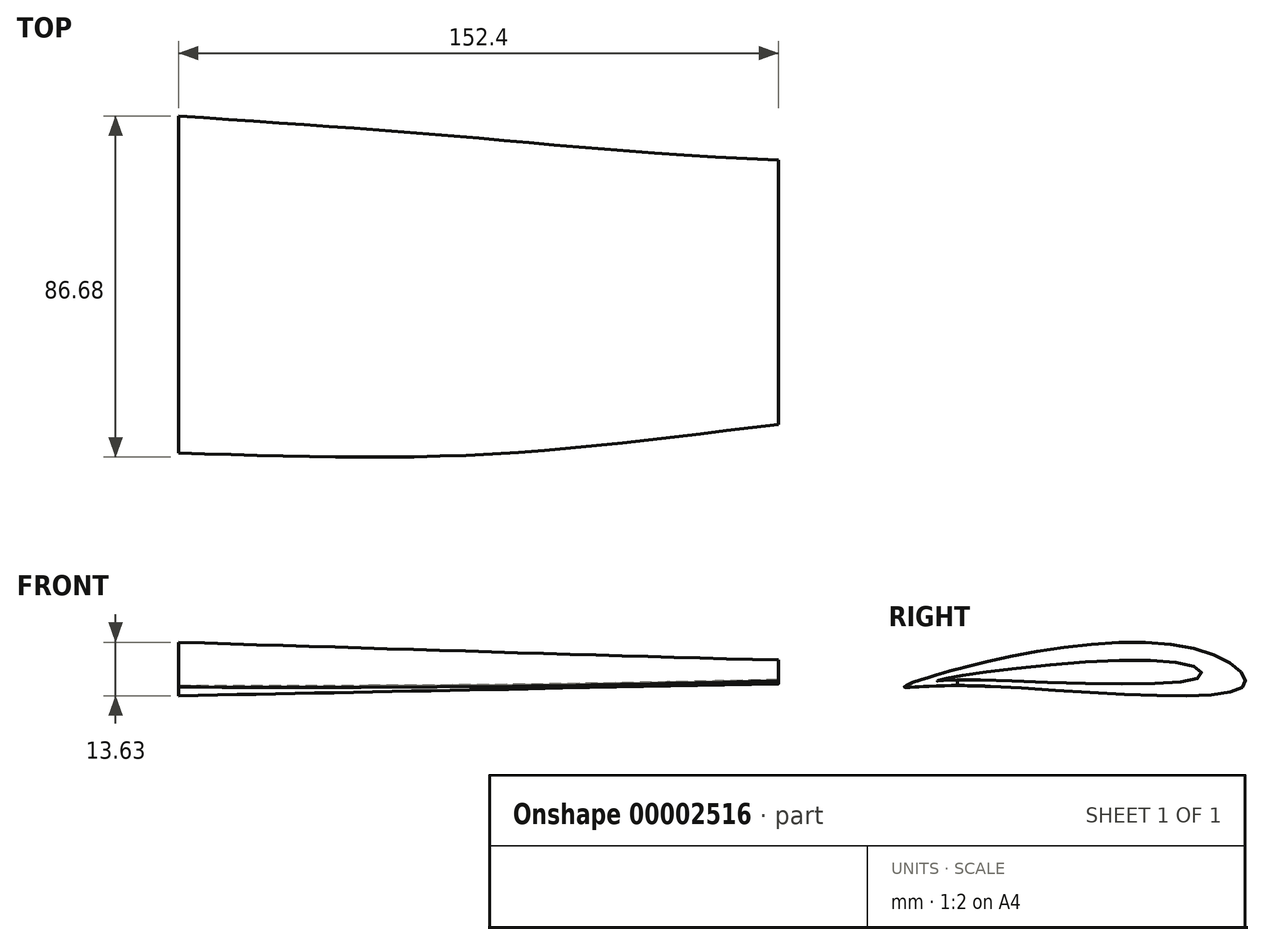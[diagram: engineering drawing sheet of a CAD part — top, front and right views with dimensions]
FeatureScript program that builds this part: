
annotation { "Feature Type Name" : "Feature", "Feature Type Description" : "" }
export const myFeature = defineFeature(function(context is Context, id is Id, definition is map)
    precondition{}
    {
        {
            var Q0;
            Q0=qCreatedBy(makeId("Right.planeOp"),FACE);
            var sketch = newSketch(context, id + "F0", { "sketchPlane" : qUnion([Q0])});
            skFitSpline(sketch, "E0", {"points": [v(-38.5, -3.54) * mm, v(34.08, -3.84) * mm, v(22.57, 5.6) * mm, v(-38.5, 0.59) * mm, v(-50.9, -3.84) * mm, v(-38.5, -3.54) * mm]});
            skSolve(sketch);
        }
        {
            var Q0;
            Q0=qCreatedBy(makeId("Right.planeOp"),FACE);
            cPlane(context, id + "F1", {"entities" : qUnion([Q0]), "cplaneType" : CPlaneType.OFFSET, "offset" : 76.2 * mm, "width" : 152.4 * mm, "height" : 152.4 * mm});
        }
        {
            var Q0;
            Q0=qCreatedBy(id+"F1.planeOp",FACE);
            var sketch = newSketch(context, id + "F2", { "sketchPlane" : qUnion([Q0])});
            skFitSpline(sketch, "E1", {"points": [v(-51.32, -3.77) * mm, v(-38.6, -3.44) * mm, v(28.57, -2.45) * mm, v(21.8, 3.33) * mm, v(-38.77, 0) * mm, v(-51.32, -3.77) * mm]});
            skSolve(sketch);
        }
        {
            var Q0;
            Q0=qCreatedBy(id+"F1.planeOp",FACE);
            cPlane(context, id + "F3", {"entities" : qUnion([Q0]), "cplaneType" : CPlaneType.OFFSET, "offset" : 76.2 * mm, "width" : 152.4 * mm, "height" : 152.4 * mm});
        }
        {
            var Q0;
            Q0=qCreatedBy(id+"F3.planeOp",FACE);
            var sketch = newSketch(context, id + "F4", { "sketchPlane" : qUnion([Q0])});
            skFitSpline(sketch, "E2", {"points": [v(-43.68, -2.43) * mm, v(-37.58, -2.14) * mm, v(22.98, -1.43) * mm, v(20.29, 1.69) * mm, v(-38.57, -1.3) * mm, v(-43.68, -2.43) * mm]});
            skSolve(sketch);
        }
        {
            var Q0;
            Q0=makeQuery(id+"F0.imprint","IMPRINT",FACE,{"disambiguationData":[TD([[makeQuery(id+"F0.imprint","IMPRINT",EDGE,{"derivedFrom":sQuery(id+"F0.wireOp",EDGE,"E0")}),1.0]])]});
            var Q1;
            Q1=makeQuery(id+"F2.imprint","IMPRINT",FACE,{"disambiguationData":[TD([[makeQuery(id+"F2.imprint","IMPRINT",EDGE,{"derivedFrom":sQuery(id+"F2.wireOp",EDGE,"E1")}),1.0]])]});
            var Q2;
            Q2=makeQuery(id+"F4.imprint","IMPRINT",FACE,{"disambiguationData":[TD([[makeQuery(id+"F4.imprint","IMPRINT",EDGE,{"derivedFrom":sQuery(id+"F4.wireOp",EDGE,"E2")}),1.0]])]});
            loft(context, id + "F5", {"sheetProfilesArray" : [{ "sheetProfileEntities" : qUnion([Q0]) }, { "sheetProfileEntities" : qUnion([Q1]) }, { "sheetProfileEntities" : qUnion([Q2]) }]});
        }
    });
